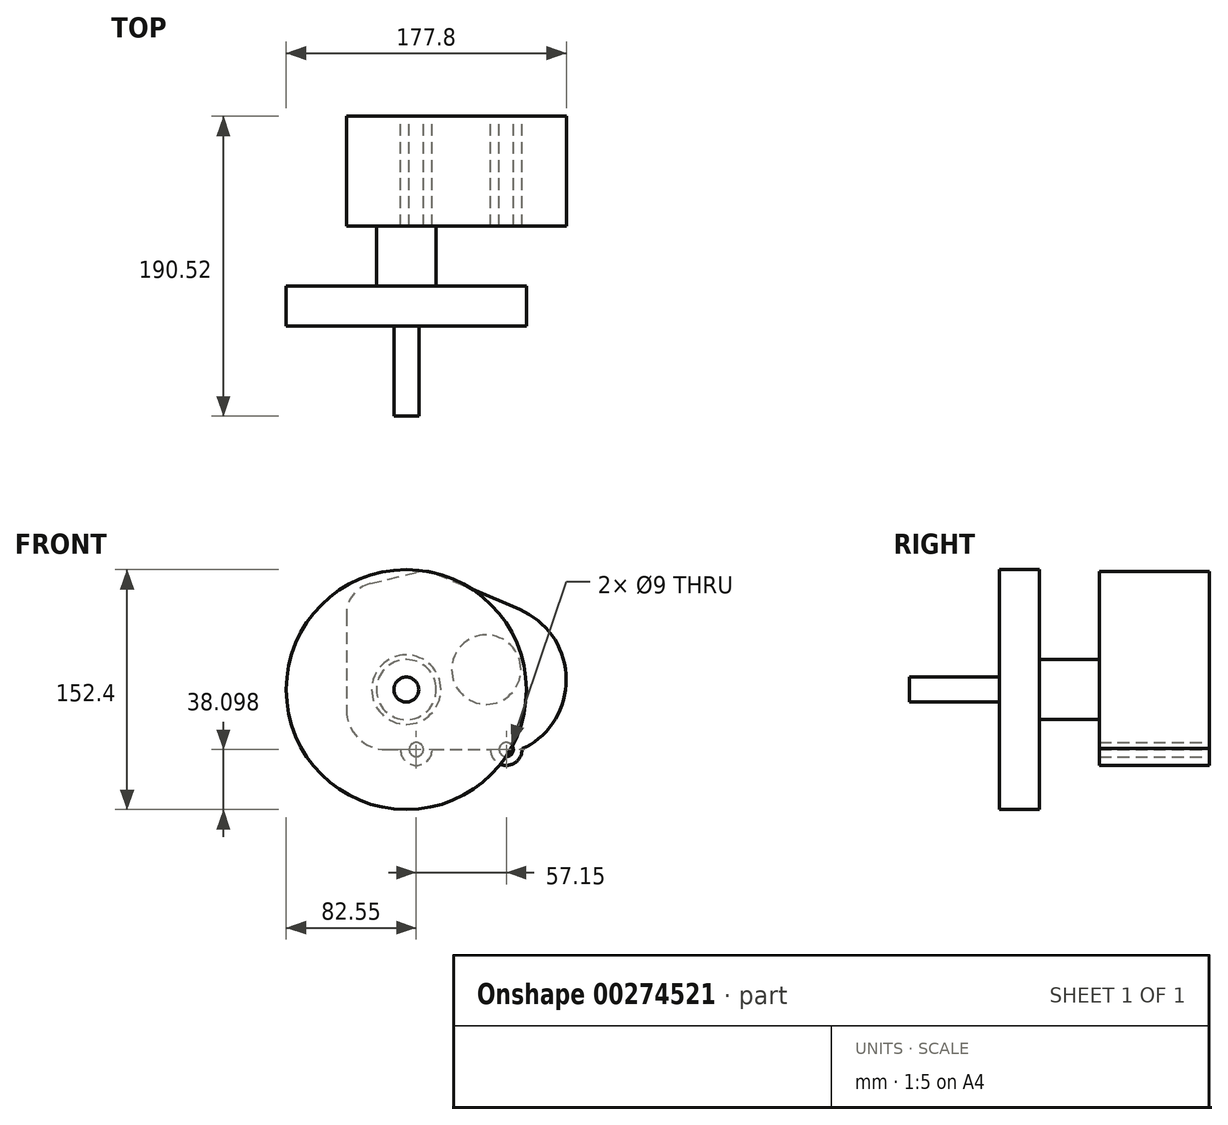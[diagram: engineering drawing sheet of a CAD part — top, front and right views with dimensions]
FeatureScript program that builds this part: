
annotation { "Feature Type Name" : "Feature", "Feature Type Description" : "" }
export const myFeature = defineFeature(function(context is Context, id is Id, definition is map)
    precondition{}
    {
        {
            var Q0;
            Q0=qCreatedBy(makeId("Front.planeOp"),FACE);
            var sketch = newSketch(context, id + "F0", { "sketchPlane" : qUnion([Q0])});
            skLineSegment(sketch, "E0", {"start": v(-47.59, 26.92) * mm, "end": v(-47.59, -33.66) * mm});
            skLineSegment(sketch, "E1", {"start": v(-22.19, -59.06) * mm, "end": v(58.63, -59.06) * mm});
            skLineSegment(sketch, "E2.0", {"start": v(-52.59, 13.31) * mm, "end": v(-52.59, -54.39) * mm});
            skLineSegment(sketch, "E3", {"start": v(-32.44, 46.33) * mm, "end": v(-3.32, 53.6) * mm});
            skLineSegment(sketch, "E4", {"start": v(9.4, 52.6) * mm, "end": v(62.6, 29.84) * mm});
            skPoint(sketch, "E5.visualSharp", {"position": v(-47.59, -59.06) * mm});
            skArc(sketch, "E5.filletArc", {"start": v(-47.59, -33.66) * mm, "mid": v(-40.15, -51.62) * mm, "end": v(-22.19, -59.06) * mm});
            skPoint(sketch, "E6.visualSharp", {"position": v(-47.59, 42.54) * mm});
            skArc(sketch, "E6.filletArc", {"start": v(-32.44, 46.33) * mm, "mid": v(-43.35, 39.23) * mm, "end": v(-47.59, 26.92) * mm});
            skPoint(sketch, "E7.visualSharp", {"position": v(3.21, 55.24) * mm});
            skArc(sketch, "E7.filletArc", {"start": v(9.4, 52.6) * mm, "mid": v(3.12, 54.14) * mm, "end": v(-3.32, 53.6) * mm});
            skPoint(sketch, "E8", {"position": v(92.11, -14.61) * mm});
            skArc(sketch, "E9", {"start": v(69.18, -56.05) * mm, "mid": v(91.97, -11.1) * mm, "end": v(62.6, 29.84) * mm});
            skPoint(sketch, "E10.visualSharp", {"position": v(63.54, -59.06) * mm});
            skArc(sketch, "E10.filletArc", {"start": v(58.63, -59.06) * mm, "mid": v(64.12, -58.3) * mm, "end": v(69.18, -56.05) * mm});
            skSolve(sketch);
        }
        {
            var Q0;
            Q0 = qSketchRegion(id + "F0", true);
            extrude(context, id + "F1", {"entities" : qUnion([Q0]), "depth" : 69.85 * mm});
        }
        {
            var Q0;
            Q0=makeQuery(id+"F1.opExtrude","CAP_FACE",FACE,{"disambiguationData":[OSD([sQuery(id+"F0.wireOp",EDGE,"E0"),sQuery(id+"F0.wireOp",EDGE,"E1"),sQuery(id+"F0.wireOp",EDGE,"E3"),sQuery(id+"F0.wireOp",EDGE,"E4"),sQuery(id+"F0.wireOp",EDGE,"E5.filletArc"),sQuery(id+"F0.wireOp",EDGE,"E6.filletArc"),sQuery(id+"F0.wireOp",EDGE,"E7.filletArc"),sQuery(id+"F0.wireOp",EDGE,"E9"),sQuery(id+"F0.wireOp",EDGE,"E10.filletArc")])],"isStart":false});
            var sketch = newSketch(context, id + "F2", { "sketchPlane" : qUnion([Q0])});
            skCircle(sketch, "E11", {"center": v(-9.49, -20.96) * mm, "radius": 22 * mm});
            skCircle(sketch, "E12", {"center": v(41.31, -8.26) * mm, "radius": 22 * mm});
            skSolve(sketch);
        }
        {
            var Q0;
            Q0 = qSketchRegion(id + "F2", true);
            extrude(context, id + "F3", {"entities" : qUnion([Q0]), "operationType" : NewBodyOperationType.ADD, "oppositeDirection" : true, "depth" : 25 / 203.2 * mm, "hasSecondDirection" : true, "secondDirectionOppositeDirection" : false, "secondDirectionDepth" : 1 / 50.8 * mm});
        }
        {
            var Q0;
            Q0=makeQuery(id+"F1.opExtrude","CAP_FACE",FACE,{"disambiguationData":[OSD([sQuery(id+"F0.wireOp",EDGE,"E0"),sQuery(id+"F0.wireOp",EDGE,"E1"),sQuery(id+"F0.wireOp",EDGE,"E3"),sQuery(id+"F0.wireOp",EDGE,"E4"),sQuery(id+"F0.wireOp",EDGE,"E5.filletArc"),sQuery(id+"F0.wireOp",EDGE,"E6.filletArc"),sQuery(id+"F0.wireOp",EDGE,"E7.filletArc"),sQuery(id+"F0.wireOp",EDGE,"E9"),sQuery(id+"F0.wireOp",EDGE,"E10.filletArc")])],"isStart":true});
            var sketch = newSketch(context, id + "F4", { "sketchPlane" : qUnion([Q0])});
            skCircle(sketch, "E13", {"center": v(-54.01, -59.06) * mm, "radius": 10 * mm});
            skCircle(sketch, "E14", {"center": v(3.14, -59.06) * mm, "radius": 10 * mm});
            skSolve(sketch);
        }
        {
            var Q0;
            Q0 = qSketchRegion(id + "F4", true);
            var Q1;
            Q1=makeQuery(id+"F1.opExtrude","CAP_FACE",FACE,{"disambiguationData":[OSD([sQuery(id+"F0.wireOp",EDGE,"E0"),sQuery(id+"F0.wireOp",EDGE,"E1"),sQuery(id+"F0.wireOp",EDGE,"E3"),sQuery(id+"F0.wireOp",EDGE,"E4"),sQuery(id+"F0.wireOp",EDGE,"E5.filletArc"),sQuery(id+"F0.wireOp",EDGE,"E6.filletArc"),sQuery(id+"F0.wireOp",EDGE,"E7.filletArc"),sQuery(id+"F0.wireOp",EDGE,"E9"),sQuery(id+"F0.wireOp",EDGE,"E10.filletArc")])],"isStart":false});
            extrude(context, id + "F5", {"entities" : qUnion([Q0]), "operationType" : NewBodyOperationType.ADD, "endBound" : BoundingType.UP_TO_SURFACE, "oppositeDirection" : true, "endBoundEntityFace" : qUnion([Q1]), "depth" : 25 * mm});
        }
        {
            var Q0;
            Q0=makeQuery(id+"F5.boolean.opBoolean","MERGE",FACE,{"derivedFrom":[makeQuery(id+"F1.opExtrude","CAP_FACE",FACE,{"disambiguationData":[OSD([sQuery(id+"F0.wireOp",EDGE,"E0"),sQuery(id+"F0.wireOp",EDGE,"E1"),sQuery(id+"F0.wireOp",EDGE,"E3"),sQuery(id+"F0.wireOp",EDGE,"E4"),sQuery(id+"F0.wireOp",EDGE,"E5.filletArc"),sQuery(id+"F0.wireOp",EDGE,"E6.filletArc"),sQuery(id+"F0.wireOp",EDGE,"E7.filletArc"),sQuery(id+"F0.wireOp",EDGE,"E9"),sQuery(id+"F0.wireOp",EDGE,"E10.filletArc")])],"isStart":true}),makeQuery(id+"F5.opExtrude","CAP_FACE",FACE,{"disambiguationData":[OSD([sQuery(id+"F4.wireOp",EDGE,"E13")])],"isStart":true}),makeQuery(id+"F5.opExtrude","CAP_FACE",FACE,{"disambiguationData":[OSD([sQuery(id+"F4.wireOp",EDGE,"E14")])],"isStart":true})]});
            var sketch = newSketch(context, id + "F6", { "sketchPlane" : qUnion([Q0])});
            skCircle(sketch, "E15", {"center": v(-54.01, -59.06) * mm, "radius": 4.5 * mm});
            skCircle(sketch, "E16", {"center": v(3.14, -59.06) * mm, "radius": 4.5 * mm});
            skSolve(sketch);
        }
        {
            var Q0;
            Q0 = qSketchRegion(id + "F6", true);
            extrude(context, id + "F7", {"entities" : qUnion([Q0]), "operationType" : NewBodyOperationType.REMOVE, "endBound" : BoundingType.THROUGH_ALL, "oppositeDirection" : true, "depth" : 25 * mm});
        }
        {
            var Q0;
            Q0=makeQuery(id+"F3.opExtrude","CAP_FACE",FACE,{"disambiguationData":[OSD([sQuery(id+"F2.wireOp",EDGE,"E11")])],"isStart":true});
            var sketch = newSketch(context, id + "F8", { "sketchPlane" : qUnion([Q0])});
            skCircle(sketch, "E17", {"center": v(-9.49, -20.96) * mm, "radius": 19.05 * mm});
            skSolve(sketch);
        }
        {
            var Q0;
            Q0 = qSketchRegion(id + "F8", true);
            extrude(context, id + "F9", {"entities" : qUnion([Q0]), "operationType" : NewBodyOperationType.ADD, "depth" : 38.1 * mm});
        }
        {
            var Q0;
            Q0=makeQuery(id+"F9.opExtrude","CAP_FACE",FACE,{"disambiguationData":[OSD([sQuery(id+"F8.wireOp",EDGE,"E17")])],"isStart":false});
            var sketch = newSketch(context, id + "F10", { "sketchPlane" : qUnion([Q0])});
            skCircle(sketch, "E18", {"center": v(-9.49, -20.96) * mm, "radius": 7.94 * mm});
            skSolve(sketch);
        }
        {
            var Q0;
            Q0 = qSketchRegion(id + "F10", true);
            extrude(context, id + "F11", {"entities" : qUnion([Q0]), "operationType" : NewBodyOperationType.ADD, "depth" : 82.55 * mm});
        }
        {
            var Q0;
            Q0=makeQuery(id+"F9.opExtrude","CAP_FACE",FACE,{"disambiguationData":[OSD([sQuery(id+"F8.wireOp",EDGE,"E17")])],"isStart":false});
            var sketch = newSketch(context, id + "F12", { "sketchPlane" : qUnion([Q0])});
            skCircle(sketch, "E19", {"center": v(-9.49, -20.96) * mm, "radius": 76.2 * mm});
            skSolve(sketch);
        }
        {
            var Q0;
            Q0 = qSketchRegion(id + "F12", true);
            extrude(context, id + "F13", {"entities" : qUnion([Q0]), "operationType" : NewBodyOperationType.ADD, "depth" : 25.4 * mm});
        }
    });
